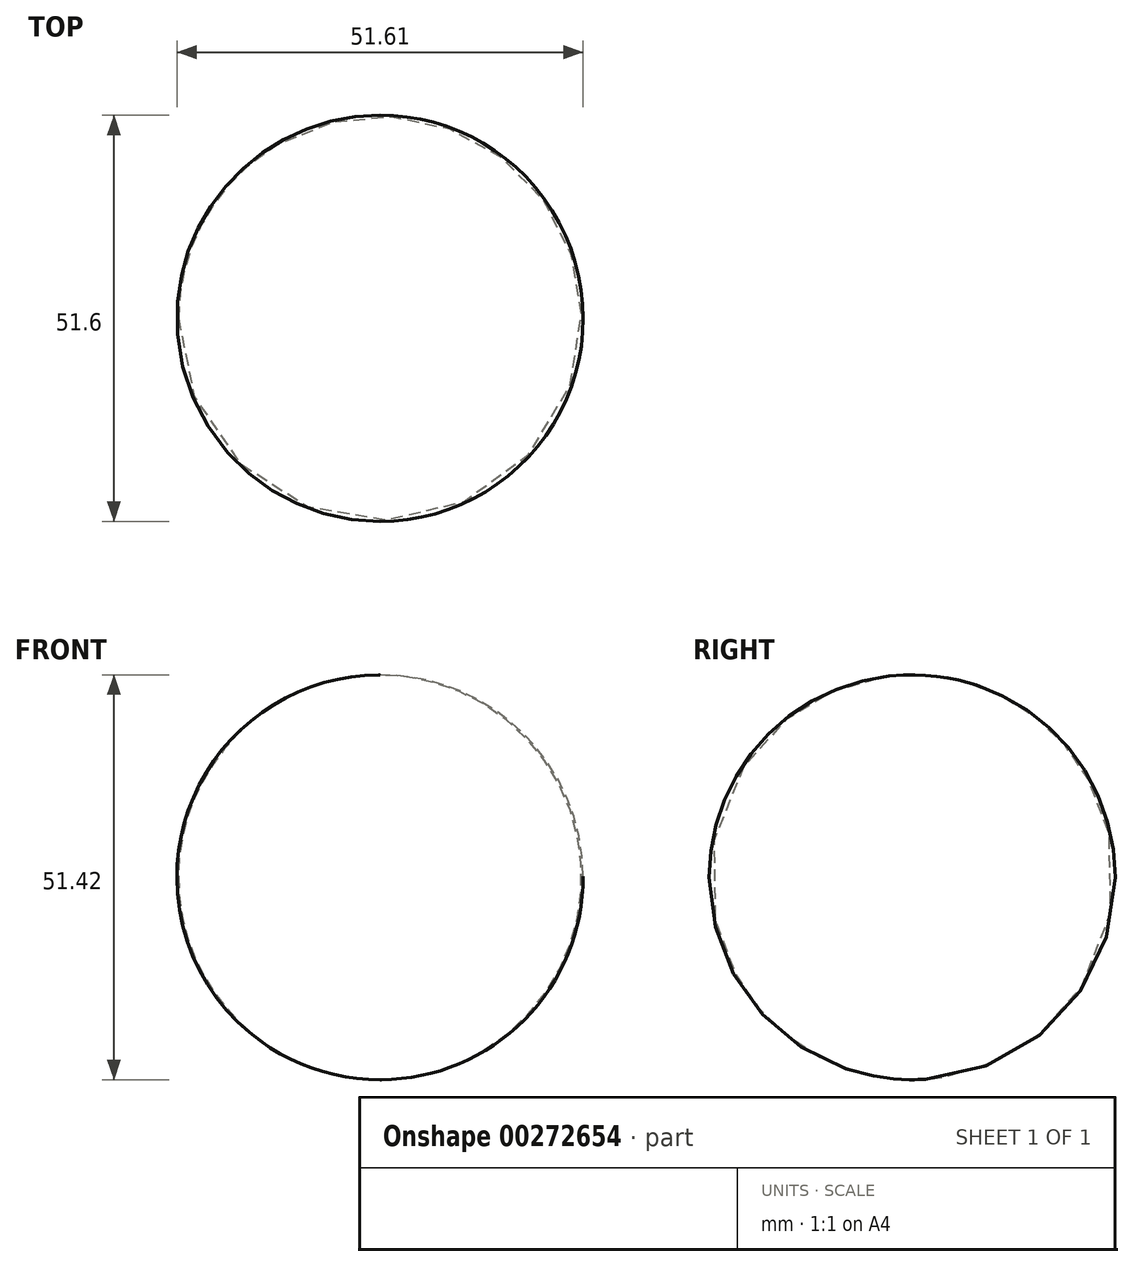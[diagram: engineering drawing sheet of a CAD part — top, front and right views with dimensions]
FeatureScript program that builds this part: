
annotation { "Feature Type Name" : "Feature", "Feature Type Description" : "" }
export const myFeature = defineFeature(function(context is Context, id is Id, definition is map)
    precondition{}
    {
        {
            var Q0;
            Q0=qCreatedBy(makeId("Front.planeOp"),FACE);
            var sketch = newSketch(context, id + "F0", { "sketchPlane" : qUnion([Q0])});
            skLineSegment(sketch, "E0", {"start": v(-0.19, 25.7) * mm, "end": v(-0.19, 25.7) * mm});
            skLineSegment(sketch, "E1", {"start": v(0, -25.7) * mm, "end": v(0, -25.7) * mm});
            skArc(sketch, "E2", {"start": v(-0.19, 25.7) * mm, "mid": v(-25.7, 0) * mm, "end": v(-0.19, -25.7) * mm});
            skLineSegment(sketch, "E3", {"start": v(-0.19, -25.7) * mm, "end": v(-0.19, -25.7) * mm});
            skArc(sketch, "E4", {"start": v(-0.19, -25.7) * mm, "mid": v(-0.1, -25.7) * mm, "end": v(0, -25.7) * mm});
            skLineSegment(sketch, "E5", {"start": v(-0.19, 25.7) * mm, "end": v(0, -25.7) * mm});
            skSolve(sketch);
        }
        {
            var Q0;
            Q0=makeQuery(id+"F0.imprint","IMPRINT",FACE,{"disambiguationData":[TD([[makeQuery(id+"F0.imprint","IMPRINT",EDGE,{"derivedFrom":sQuery(id+"F0.wireOp",EDGE,"E2")}),1.0]])]});
            var Q1;
            Q1=sQuery(id+"F0.wireOp",EDGE,"E5");
            revolve(context, id + "F1", {"entities" : qUnion([Q0]), "axis" : qUnion([Q1]), "revolveType" : RevolveType.FULL});
        }
    });
